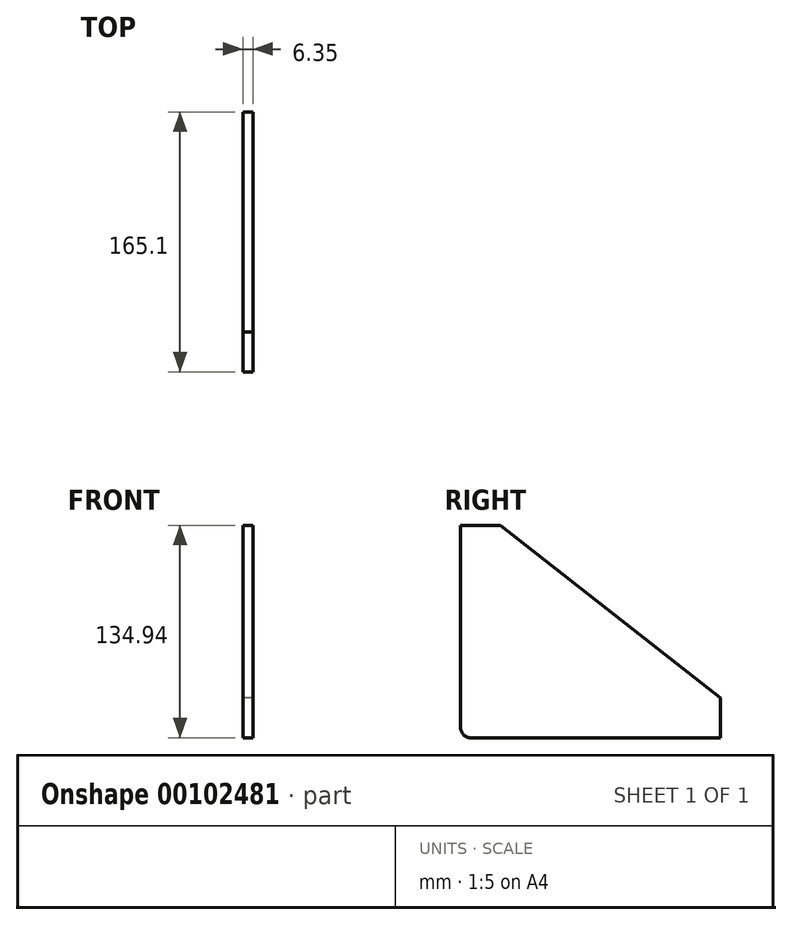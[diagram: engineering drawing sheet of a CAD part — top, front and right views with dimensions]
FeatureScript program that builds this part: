
annotation { "Feature Type Name" : "Feature", "Feature Type Description" : "" }
export const myFeature = defineFeature(function(context is Context, id is Id, definition is map)
    precondition{}
    {
        {
            var Q0;
            Q0=qCreatedBy(makeId("Right.planeOp"),FACE);
            var sketch = newSketch(context, id + "F0", { "sketchPlane" : qUnion([Q0])});
            skLineSegment(sketch, "E0", {"start": v(-82.55, 67.47) * mm, "end": v(-57.15, 67.47) * mm});
            skLineSegment(sketch, "E1", {"start": v(82.55, -67.47) * mm, "end": v(82.55, -42.07) * mm});
            skLineSegment(sketch, "E2", {"start": v(-57.15, 67.47) * mm, "end": v(82.55, -42.07) * mm});
            skLineSegment(sketch, "E3", {"start": v(-76.2, -67.47) * mm, "end": v(82.55, -67.47) * mm});
            skLineSegment(sketch, "E4", {"start": v(-82.55, 67.47) * mm, "end": v(-82.55, -61.12) * mm});
            skArc(sketch, "E5", {"start": v(-82.55, -61.12) * mm, "mid": v(-80.7, -65.6) * mm, "end": v(-76.2, -67.47) * mm});
            skSolve(sketch);
        }
        {
            var Q0;
            Q0 = qSketchRegion(id + "F0", true);
            extrude(context, id + "F1", {"entities" : qUnion([Q0]), "depth" : 6.35 * mm});
        }
    });
